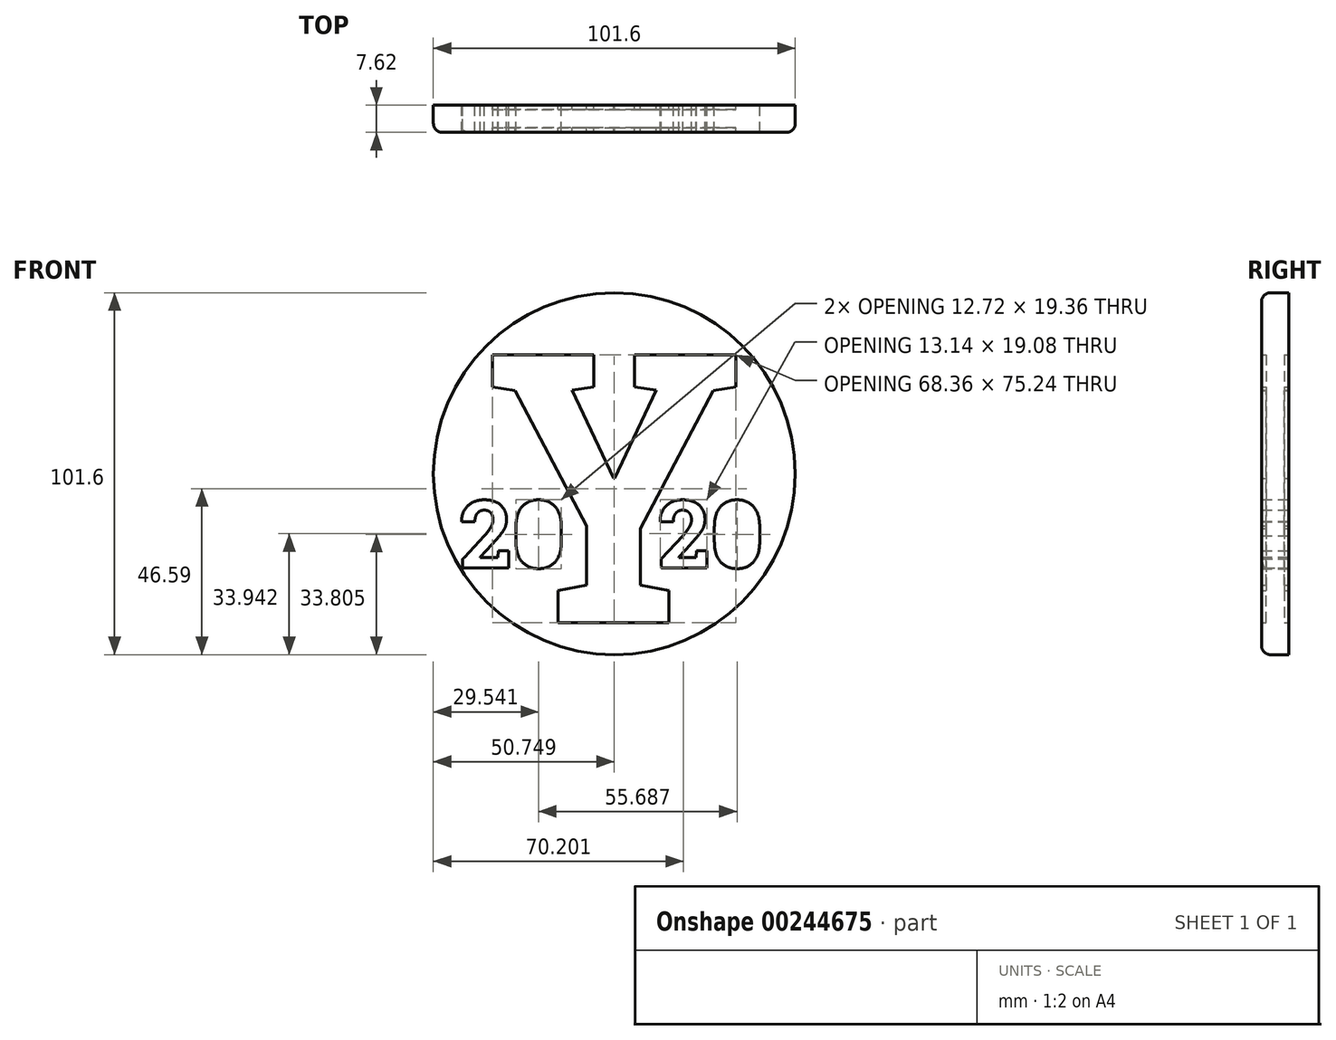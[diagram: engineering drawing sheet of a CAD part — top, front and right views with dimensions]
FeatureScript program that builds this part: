
annotation { "Feature Type Name" : "Feature", "Feature Type Description" : "" }
export const myFeature = defineFeature(function(context is Context, id is Id, definition is map)
    precondition{}
    {
        {
            var Q0;
            Q0=qCreatedBy(makeId("Front.planeOp"),FACE);
            var sketch = newSketch(context, id + "F0", { "sketchPlane" : qUnion([Q0])});
            skCircle(sketch, "E0", {"center": v(0, 0) * mm, "radius": 50.8 * mm});
            skText(sketch, "E1", { "text": "Y", "fontName": "RobotoSlab-Bold.ttf"});
            skText(sketch, "E2", { "text": "20    20", "fontName": "RobotoSlab-Bold.ttf"});
            const initialGuessF0  = {"E1": [-0.0361, -0.04183, 1, 0, 0.0762], "E2": [-0.0435, -0.0264, 1, 0, 0.01905]};
            skSetInitialGuess(sketch, initialGuessF0);
            skSolve(sketch);
        }
        {
            var Q0;
            Q0=makeQuery(id+"F0.imprint","IMPRINT",FACE,{"disambiguationData":[TD([[makeQuery(id+"F0.imprint","IMPRINT",EDGE,{"derivedFrom":sQuery(id+"F0.wireOp",EDGE,"E1.sketch_text.stroke-0")}),-1.0]])]});
            extrude(context, id + "F1", {"entities" : qUnion([Q0]), "endBound" : BoundingType.SYMMETRIC, "depth" : 5.08 * mm});
        }
        {
            var Q0;
            Q0 = qSketchRegion(id + "F0", true);
            extrude(context, id + "F2", {"entities" : qUnion([Q0]), "operationType" : NewBodyOperationType.ADD, "endBound" : BoundingType.SYMMETRIC, "depth" : 7.62 * mm});
        }
        {
            var Q0;
            Q0=makeQuery(id+"F2.opExtrude","CAP_EDGE",EDGE,{"disambiguationData":[OSD([sQuery(id+"F0.wireOp",EDGE,"E0")])],"isStart":false});
            fillet(context, id + "F3", {"entities" : qUnion([Q0]), "radius" : 2.54 * mm, "tangentPropagation" : true, "allowEdgeOverflow" : false});
        }
    });
